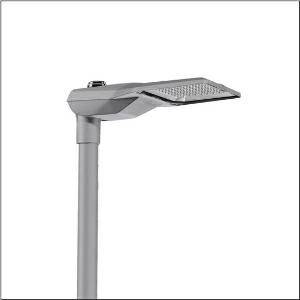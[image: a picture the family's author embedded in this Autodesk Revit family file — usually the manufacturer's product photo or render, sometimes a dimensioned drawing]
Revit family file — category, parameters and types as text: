
# Revit family: streetlight_sl_21_midi___stw1_0a_5xe7e37n08nb_3567
name_source: partatom
category: Lighting Fixtures
units: mm (PartAtom-declared; Revit-internal decimal feet)

## family parameters
Cut with Voids When Loaded = No
Host = Face
Light Source = No
Part Type = Normal
Room Calculation Point = No
Round Connector Dimension = Use Diameter
Shared = No

## types (1)
- --- (1 x LED, 22700 lm, 151.2 W, 3000K)
    Apparent Load = 151 VA
    CIE Flux Codes = 39 75 98 100 100
    Color Rendering = 70
    Color Temperature = 3000K
    Default Elevation = 1800 mm
    Description = Streetlight SL 21 midi, mast luminaire, primary light control with lens, of PMMA, primary optical cover: cover, of toughened safety glass, transparent, light distribution: STW1.0a, light emission: direct distribution, primary light characteristic: asymmetric, installation type: side-entry, LED, 3G 2.5mm², High Power LED, rated luminous flux: 22.700lm, luminous efficacy: 150lm/W, light colour: 730, colour temperature: 3000K, control: overheat protection, presetting dimming linear, constant luminous flux control, time-dependent luminous flux control, flexible luminous flux parameterisation, mains connection: 220..240V, AC, 50/60Hz, connection cable pre-assembled, cable length: 12,5m, wiring characteristics: H05VV-F, start of lifetime: 151W, end of service life: 157W, reduction: 70W, luminaire housing, of diecast aluminium (EN AC-44300), powder-coated, Siteco® metallic grey (DB 702S), corrosivity category C5 mid according to DIN EN ISO 12944, multi-level sealing system, sealing non-destructively replaceable, inclination adjustable: 0°, 5°, 10°, 15°, length: 644mm, width: 335mm, height: 110mm, spigot size: 42mm (side-entry), protection rating (complete): IP66, insulation class (complete): insulation class I (protective earthing), certification: CE, ENEC, ENEC+, VDE, impact resistance: IK09, permissible operating ambient temperature for outdoor applications: -40..+50°C, standard-compliant lighting for roads and squares, packaging unit: 1 piece

Light Distribution: STW1.0a
    Height = 111 mm
    Lamp = 1 x LED
    Lamp Light Flux = 22700 lm
    Lamp Power = 151.2 W
    Lamp count = 1
    Length = 644 mm
    Luminous efficacy = 150 lm/W
    Manufacturer = Siteco
    ModVariant = No
    Model = 5XE7E37N08NB
    Number of Poles = 1
    OnlyDefault = Yes
    Power Factor = 1
    Product Name = Streetlight SL 21 midi | STW1.0a
    Product group = mast luminaire | pylon top
    ProductGroupID = 6100
    Protection Class = Protection class I
    Protection Degree = IP 66
    RLX_Detail_Level = 1
    RLX_Emergency_Light_Flux = 0 lm
    RLX_Emergency_Type = 0
    RLX_Emergency_Type_DB = No
    RlxData = <blob elided: 90197 chars, md5=f100d74b>
    Socket = socket
    Standby Power = 0 W
    System Light Flux = 22700 lm
    System Power = 151 W
    Type Comments = factory setting: luminous flux: 100 % | dim-lin: 254 | 802 mA
    Type Image = l_1294377.jpg
    URL = http://relux.com
    VarID = @adj_084311
    Voltage = 0 V
    Weight = 0.00 kg
    Width = 336 mm

## geometry (parser evidence)
native form markers: Blend x4, Sweep x11
no freeform markers — native parametric forms only
